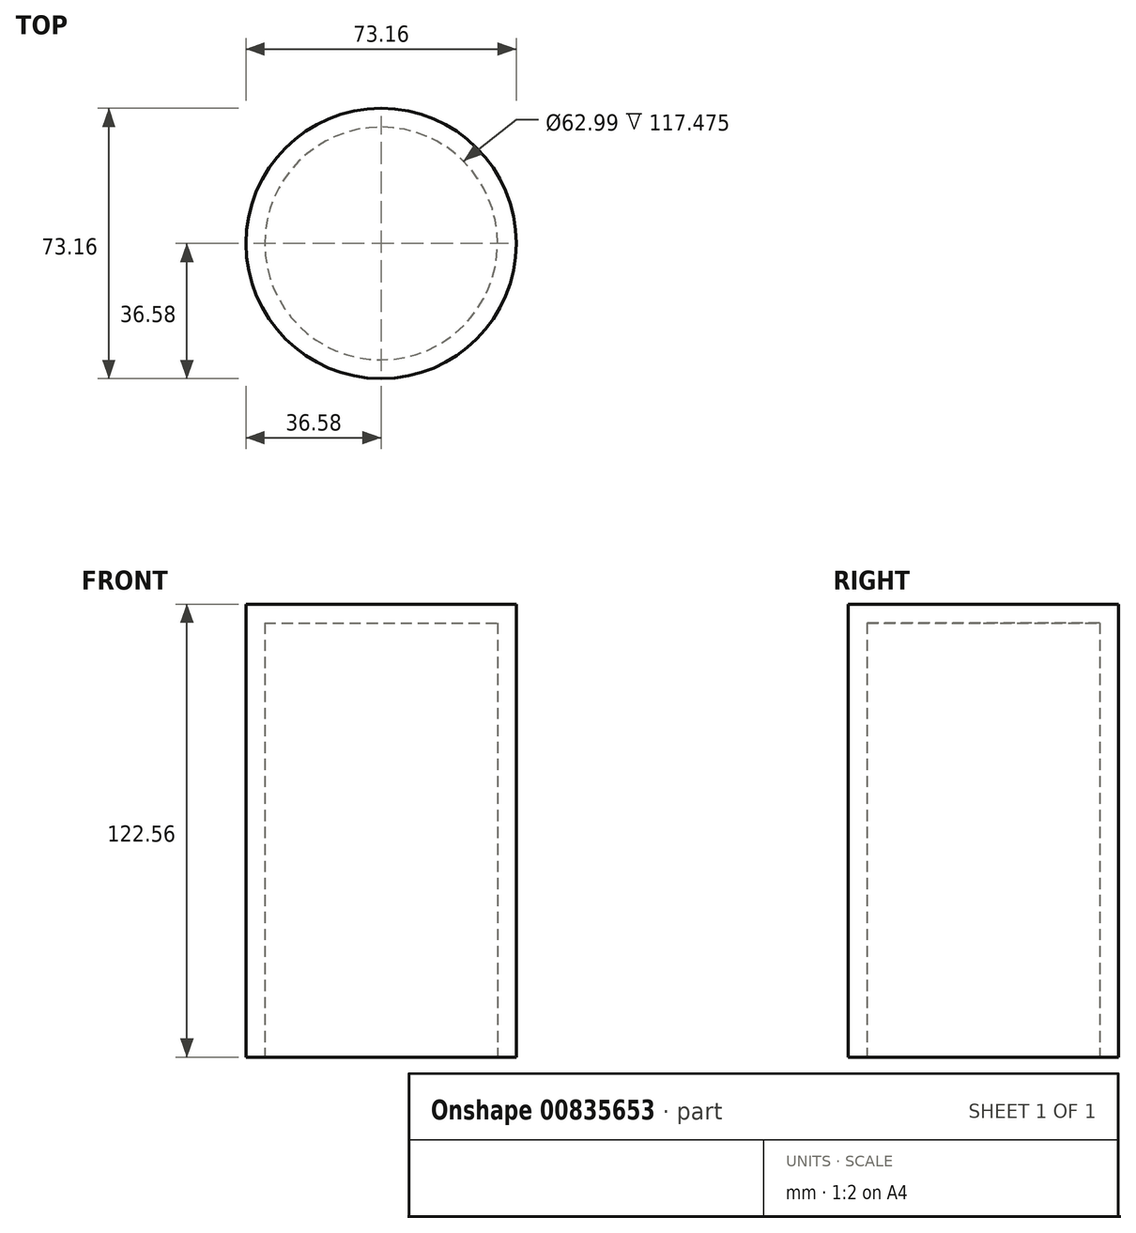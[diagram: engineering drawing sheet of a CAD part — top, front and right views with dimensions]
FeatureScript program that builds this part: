
annotation { "Feature Type Name" : "Feature", "Feature Type Description" : "" }
export const myFeature = defineFeature(function(context is Context, id is Id, definition is map)
    precondition{}
    {
        {
            var Q0;
            Q0=qCreatedBy(makeId("Top.planeOp"),FACE);
            var sketch = newSketch(context, id + "F0", { "sketchPlane" : qUnion([Q0])});
            skCircle(sketch, "E0", {"center": v(0, 0) * mm, "radius": 31.5 * mm});
            skSolve(sketch);
        }
        {
            var Q0;
            Q0=qCreatedBy(makeId("Top.planeOp"),FACE);
            var sketch = newSketch(context, id + "F1", { "sketchPlane" : qUnion([Q0])});
            skCircle(sketch, "E1", {"center": v(0, 0) * mm, "radius": 36.58 * mm});
            skSolve(sketch);
        }
        {
            var Q0;
            Q0=makeQuery(id+"F1.imprint","IMPRINT",FACE,{"disambiguationData":[TD([[makeQuery(id+"F1.imprint","IMPRINT",EDGE,{"derivedFrom":sQuery(id+"F1.wireOp",EDGE,"E1")}),1.0]])]});
            var Q1;
            Q1=sQuery(id+"F0.wireOp",EDGE,"E0");
            var Q2;
            Q2=sQuery(id+"F1.wireOp",EDGE,"E1");
            extrude(context, id + "F2", {"entities" : qUnion([Q0]), "surfaceEntities" : qUnion([Q1, Q2]), "depth" : 122.55 * mm, "offsetDistance" : 25.4 * mm});
        }
        {
            var Q0;
            Q0=makeQuery(id+"F2.opExtrude","CAP_FACE",FACE,{"disambiguationData":[OSD([sQuery(id+"F1.wireOp",EDGE,"E1")])],"isStart":true});
            var sketch = newSketch(context, id + "F3", { "sketchPlane" : qUnion([Q0])});
            skCircle(sketch, "E2", {"center": v(0, 0) * mm, "radius": 31.5 * mm});
            skSolve(sketch);
        }
        {
            var Q0;
            Q0=makeQuery(id+"F3.imprint","IMPRINT",FACE,{"disambiguationData":[TD([[makeQuery(id+"F3.imprint","IMPRINT",EDGE,{"derivedFrom":sQuery(id+"F3.wireOp",EDGE,"E2")}),1.0]])]});
            extrude(context, id + "F4", {"entities" : qUnion([Q0]), "operationType" : NewBodyOperationType.REMOVE, "oppositeDirection" : true, "depth" : 117.47 * mm, "offsetDistance" : 25.4 * mm});
        }
    });
